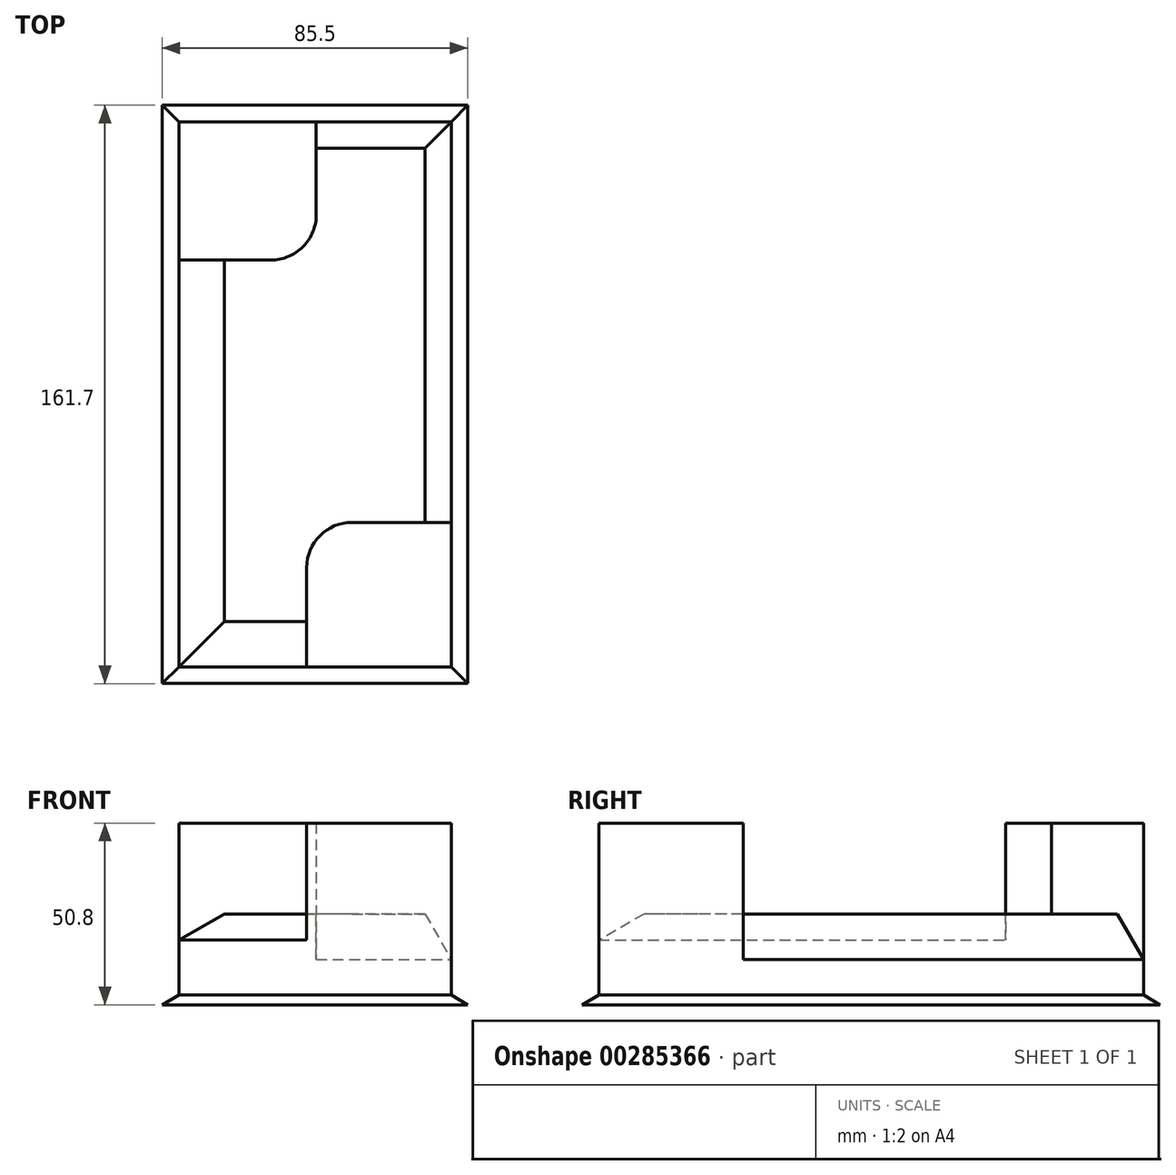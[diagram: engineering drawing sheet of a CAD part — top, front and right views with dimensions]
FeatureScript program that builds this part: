
annotation { "Feature Type Name" : "Feature", "Feature Type Description" : "" }
export const myFeature = defineFeature(function(context is Context, id is Id, definition is map)
    precondition{}
    {
        {
            var Q0;
            Q0=qCreatedBy(makeId("Top.planeOp"),FACE);
            var sketch = newSketch(context, id + "F0", { "sketchPlane" : qUnion([Q0])});
            skLineSegment(sketch, "E0.bottom", {"start": v(-34.93, 85.72) * mm, "end": v(53.97, 85.72) * mm});
            skLineSegment(sketch, "E0.top", {"start": v(-34.93, -79.38) * mm, "end": v(53.97, -79.38) * mm});
            skLineSegment(sketch, "E0.left", {"start": v(-34.93, 85.72) * mm, "end": v(-34.93, -79.38) * mm});
            skLineSegment(sketch, "E0.right", {"start": v(53.97, 85.72) * mm, "end": v(53.97, -79.38) * mm});
            skLineSegment(sketch, "E1.0", {"start": v(-28.58, 79.37) * mm, "end": v(47.62, 79.37) * mm});
            skLineSegment(sketch, "E1.1", {"start": v(-28.58, 79.37) * mm, "end": v(-28.58, -73.03) * mm});
            skLineSegment(sketch, "E1.2", {"start": v(-28.58, -73.03) * mm, "end": v(47.62, -73.03) * mm});
            skLineSegment(sketch, "E1.3", {"start": v(47.62, 79.37) * mm, "end": v(47.62, -73.03) * mm});
            skLineSegment(sketch, "E2", {"start": v(-28.58, 40.73) * mm, "end": v(-2.82, 40.73) * mm});
            skLineSegment(sketch, "E3", {"start": v(9.88, 79.37) * mm, "end": v(9.88, 53.62) * mm});
            skArc(sketch, "E4", {"start": v(-2.82, 40.73) * mm, "mid": v(6.22, 44.52) * mm, "end": v(9.88, 53.62) * mm});
            skLineSegment(sketch, "E5", {"start": v(7.2, -73.03) * mm, "end": v(7.2, -45.3) * mm});
            skLineSegment(sketch, "E6", {"start": v(47.62, -32.6) * mm, "end": v(19.9, -32.6) * mm});
            skArc(sketch, "E7", {"start": v(19.9, -32.6) * mm, "mid": v(10.91, -36.32) * mm, "end": v(7.2, -45.3) * mm});
            skSolve(sketch);
        }
        {
            var Q0;
            Q0=makeQuery(id+"F0.imprint","IMPRINT",FACE,{"disambiguationData":[TD([[makeQuery(id+"F0.imprint","IMPRINT",EDGE,{"derivedFrom":sQuery(id+"F0.wireOp",EDGE,"E0.bottom")}),-1.0]])]});
            extrude(context, id + "F1", {"entities" : qUnion([Q0]), "depth" : 6.35 * mm});
        }
        {
            var Q0;
            {var subQ4=sQuery(id+"F0.wireOp",EDGE,"E2");Q0=makeQuery(id+"F0.imprint","IMPRINT",FACE,{"disambiguationData":[TD([[makeQuery(id+"F0.imprint","IMPRINT",EDGE,{"derivedFrom":subQ4}),-1.0]])]});}
            extrude(context, id + "F2", {"entities" : qUnion([Q0]), "operationType" : NewBodyOperationType.ADD, "depth" : 25.4 * mm});
        }
        {
            var Q0;
            {var subQ1=sQuery(id+"F0.wireOp",EDGE,"E2");Q0=makeQuery(id+"F0.imprint","IMPRINT",FACE,{"disambiguationData":[TD([[makeQuery(id+"F0.imprint","IMPRINT",EDGE,{"derivedFrom":subQ1}),1.0]])]});}
            var Q1;
            {var subQ0=sQuery(id+"F0.wireOp",EDGE,"E5");Q1=makeQuery(id+"F0.imprint","IMPRINT",FACE,{"disambiguationData":[TD([[makeQuery(id+"F0.imprint","IMPRINT",EDGE,{"derivedFrom":subQ0}),-1.0]])]});}
            extrude(context, id + "F3", {"entities" : qUnion([Q0, Q1]), "operationType" : NewBodyOperationType.ADD, "depth" : 25.4 * mm});
        }
        {
            var Q0;
            Q0=makeQuery(id+"F1.opExtrude","CAP_EDGE",EDGE,{"disambiguationData":[OSD([sQuery(id+"F0.wireOp",EDGE,"E0.top")])],"isStart":false});
            var Q1;
            Q1=makeQuery(id+"F1.opExtrude","CAP_EDGE",EDGE,{"disambiguationData":[OSD([sQuery(id+"F0.wireOp",EDGE,"E0.right")])],"isStart":false});
            var Q2;
            Q2=makeQuery(id+"F1.opExtrude","CAP_EDGE",EDGE,{"disambiguationData":[OSD([sQuery(id+"F0.wireOp",EDGE,"E0.left")])],"isStart":false});
            var Q3;
            Q3=makeQuery(id+"F1.opExtrude","CAP_EDGE",EDGE,{"disambiguationData":[OSD([sQuery(id+"F0.wireOp",EDGE,"E0.bottom")])],"isStart":false});
            var Q4;
            Q4=makeQuery(id+"F2.opExtrude","CAP_EDGE",EDGE,{"disambiguationData":[OSD([sQuery(id+"F0.wireOp",EDGE,"E1.2")])],"isStart":false});
            var Q5;
            Q5=makeQuery(id+"F2.opExtrude","CAP_EDGE",EDGE,{"disambiguationData":[OSD([sQuery(id+"F0.wireOp",EDGE,"E1.1")])],"isStart":false});
            var Q6;
            Q6=makeQuery(id+"F2.opExtrude","CAP_EDGE",EDGE,{"disambiguationData":[OSD([sQuery(id+"F0.wireOp",EDGE,"E1.0")])],"isStart":false});
            var Q7;
            Q7=makeQuery(id+"F2.opExtrude","CAP_EDGE",EDGE,{"disambiguationData":[OSD([sQuery(id+"F0.wireOp",EDGE,"E1.3")])],"isStart":false});
            chamfer(context, id + "F4", {"entities" : qUnion([Q0, Q1, Q2, Q3, Q4, Q5, Q6, Q7]), "chamferType" : ChamferType.OFFSET_ANGLE, "width" : 12.7 * mm, "oppositeDirection" : false, "angle" : 30 * degree, "tangentPropagation" : true});
        }
        {
            var Q0;
            {var subQ0=sQuery(id+"F0.wireOp",EDGE,"E5");Q0=makeQuery(id+"F0.imprint","IMPRINT",FACE,{"disambiguationData":[TD([[makeQuery(id+"F0.imprint","IMPRINT",EDGE,{"derivedFrom":subQ0}),-1.0]])]});}
            var Q1;
            {var subQ1=sQuery(id+"F0.wireOp",EDGE,"E2");Q1=makeQuery(id+"F0.imprint","IMPRINT",FACE,{"disambiguationData":[TD([[makeQuery(id+"F0.imprint","IMPRINT",EDGE,{"derivedFrom":subQ1}),1.0]])]});}
            extrude(context, id + "F5", {"entities" : qUnion([Q0, Q1]), "operationType" : NewBodyOperationType.ADD, "depth" : 50.8 * mm});
        }
    });
